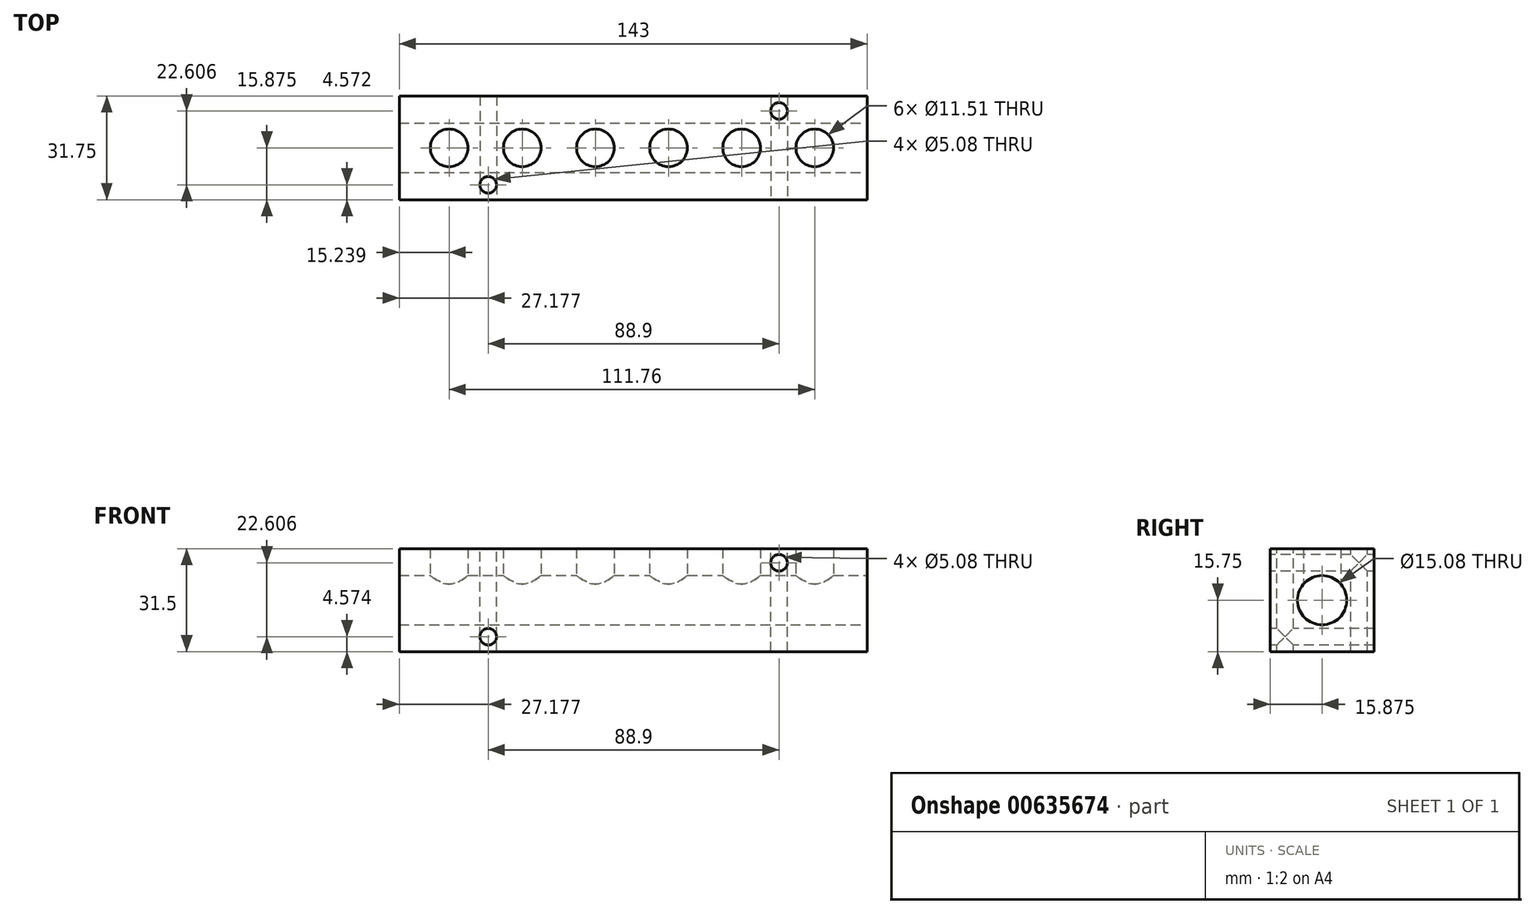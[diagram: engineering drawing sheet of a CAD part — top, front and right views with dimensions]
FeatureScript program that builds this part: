
annotation { "Feature Type Name" : "Feature", "Feature Type Description" : "" }
export const myFeature = defineFeature(function(context is Context, id is Id, definition is map)
    precondition{}
    {
        {
            var Q0;
            Q0=qCreatedBy(makeId("Front.planeOp"),FACE);
            var sketch = newSketch(context, id + "F0", { "sketchPlane" : qUnion([Q0])});
            skLineSegment(sketch, "E0.bottom", {"start": v(71.5, -15.75) * mm, "end": v(-71.5, -15.75) * mm});
            skLineSegment(sketch, "E0.top", {"start": v(71.5, 15.75) * mm, "end": v(-71.5, 15.75) * mm});
            skLineSegment(sketch, "E0.left", {"start": v(71.5, -15.75) * mm, "end": v(71.5, 15.75) * mm});
            skLineSegment(sketch, "E0.right", {"start": v(-71.5, -15.75) * mm, "end": v(-71.5, 15.75) * mm});
            skPoint(sketch, "E0.middle", {"position": v(0, 0) * mm});
            skSolve(sketch);
        }
        {
            var Q0;
            Q0=qSketchRegion(id+"F0",true);
            extrude(context, id + "F1", {"entities" : qUnion([Q0]), "oppositeDirection" : true, "depth" : 31.75 * mm});
        }
        {
            var Q0;
            Q0=qCreatedBy(makeId("Top.planeOp"),FACE);
            var sketch = newSketch(context, id + "F2", { "sketchPlane" : qUnion([Q0])});
            skLineSegment(sketch, "E1", {"start": v(-71.5, 15.88) * mm, "end": v(71.5, 15.88) * mm, "construction": true});
            skPoint(sketch, "E2", {"position": v(-56.26, 15.88) * mm});
            skPoint(sketch, "E3", {"position": v(-33.9, 15.88) * mm});
            skPoint(sketch, "E4", {"position": v(-11.56, 15.88) * mm});
            skPoint(sketch, "E5", {"position": v(10.8, 15.88) * mm});
            skPoint(sketch, "E6", {"position": v(33.15, 15.88) * mm});
            skPoint(sketch, "E7", {"position": v(55.5, 15.88) * mm});
            skCircle(sketch, "E8", {"center": v(-56.26, 15.88) * mm, "radius": 5.75 * mm});
            skCircle(sketch, "E9", {"center": v(-33.9, 15.88) * mm, "radius": 5.75 * mm});
            skCircle(sketch, "E10", {"center": v(-11.56, 15.88) * mm, "radius": 5.75 * mm});
            skCircle(sketch, "E11", {"center": v(10.8, 15.88) * mm, "radius": 5.75 * mm});
            skCircle(sketch, "E12", {"center": v(33.15, 15.88) * mm, "radius": 5.75 * mm});
            skCircle(sketch, "E13", {"center": v(55.5, 15.88) * mm, "radius": 5.75 * mm});
            skSolve(sketch);
        }
        {
            var Q0;
            Q0=qSketchRegion(id+"F2",true);
            extrude(context, id + "F3", {"entities" : qUnion([Q0]), "operationType" : NewBodyOperationType.REMOVE, "depth" : 15.88 * mm});
        }
        {
            var Q0;
            Q0=makeQuery(id+"F1.opExtrude","SWEPT_FACE",FACE,{"disambiguationData":[OSD([sQuery(id+"F0.wireOp",EDGE,"E0.left")])]});
            var sketch = newSketch(context, id + "F4", { "sketchPlane" : qUnion([Q0])});
            skLineSegment(sketch, "E14", {"start": v(0, 15.75) * mm, "end": v(31.75, -15.75) * mm, "construction": true});
            skCircle(sketch, "E15", {"center": v(15.88, 0) * mm, "radius": 7.54 * mm});
            skSolve(sketch);
        }
        {
            var Q0;
            Q0=qSketchRegion(id+"F4",true);
            extrude(context, id + "F5", {"entities" : qUnion([Q0]), "operationType" : NewBodyOperationType.REMOVE, "endBound" : BoundingType.THROUGH_ALL, "oppositeDirection" : true, "depth" : 25.4 * mm});
        }
        {
            var Q0;
            Q0=makeQuery(id+"F1.opExtrude","CAP_FACE",FACE,{"disambiguationData":[OSD([sQuery(id+"F0.wireOp",EDGE,"E0.bottom"),sQuery(id+"F0.wireOp",EDGE,"E0.top"),sQuery(id+"F0.wireOp",EDGE,"E0.left"),sQuery(id+"F0.wireOp",EDGE,"E0.right")])],"isStart":true});
            var sketch = newSketch(context, id + "F6", { "sketchPlane" : qUnion([Q0])});
            skCircle(sketch, "E16", {"center": v(-44.32, -11.18) * mm, "radius": 2.54 * mm});
            skCircle(sketch, "E17", {"center": v(44.58, 11.43) * mm, "radius": 2.54 * mm});
            skSolve(sketch);
        }
        {
            var Q0;
            Q0=qSketchRegion(id+"F6",true);
            extrude(context, id + "F7", {"entities" : qUnion([Q0]), "operationType" : NewBodyOperationType.REMOVE, "endBound" : BoundingType.THROUGH_ALL, "oppositeDirection" : true, "depth" : 25.4 * mm});
        }
        {
            var Q0;
            Q0=makeQuery(id+"F1.opExtrude","SWEPT_FACE",FACE,{"disambiguationData":[OSD([sQuery(id+"F0.wireOp",EDGE,"E0.top")])]});
            var sketch = newSketch(context, id + "F8", { "sketchPlane" : qUnion([Q0])});
            skCircle(sketch, "E18", {"center": v(44.58, 27.18) * mm, "radius": 2.54 * mm});
            skCircle(sketch, "E19", {"center": v(-44.32, 4.57) * mm, "radius": 2.54 * mm});
            skSolve(sketch);
        }
        {
            var Q0;
            Q0=qSketchRegion(id+"F8",true);
            extrude(context, id + "F9", {"entities" : qUnion([Q0]), "operationType" : NewBodyOperationType.REMOVE, "endBound" : BoundingType.THROUGH_ALL, "oppositeDirection" : true, "depth" : 25.4 * mm});
        }
    });
